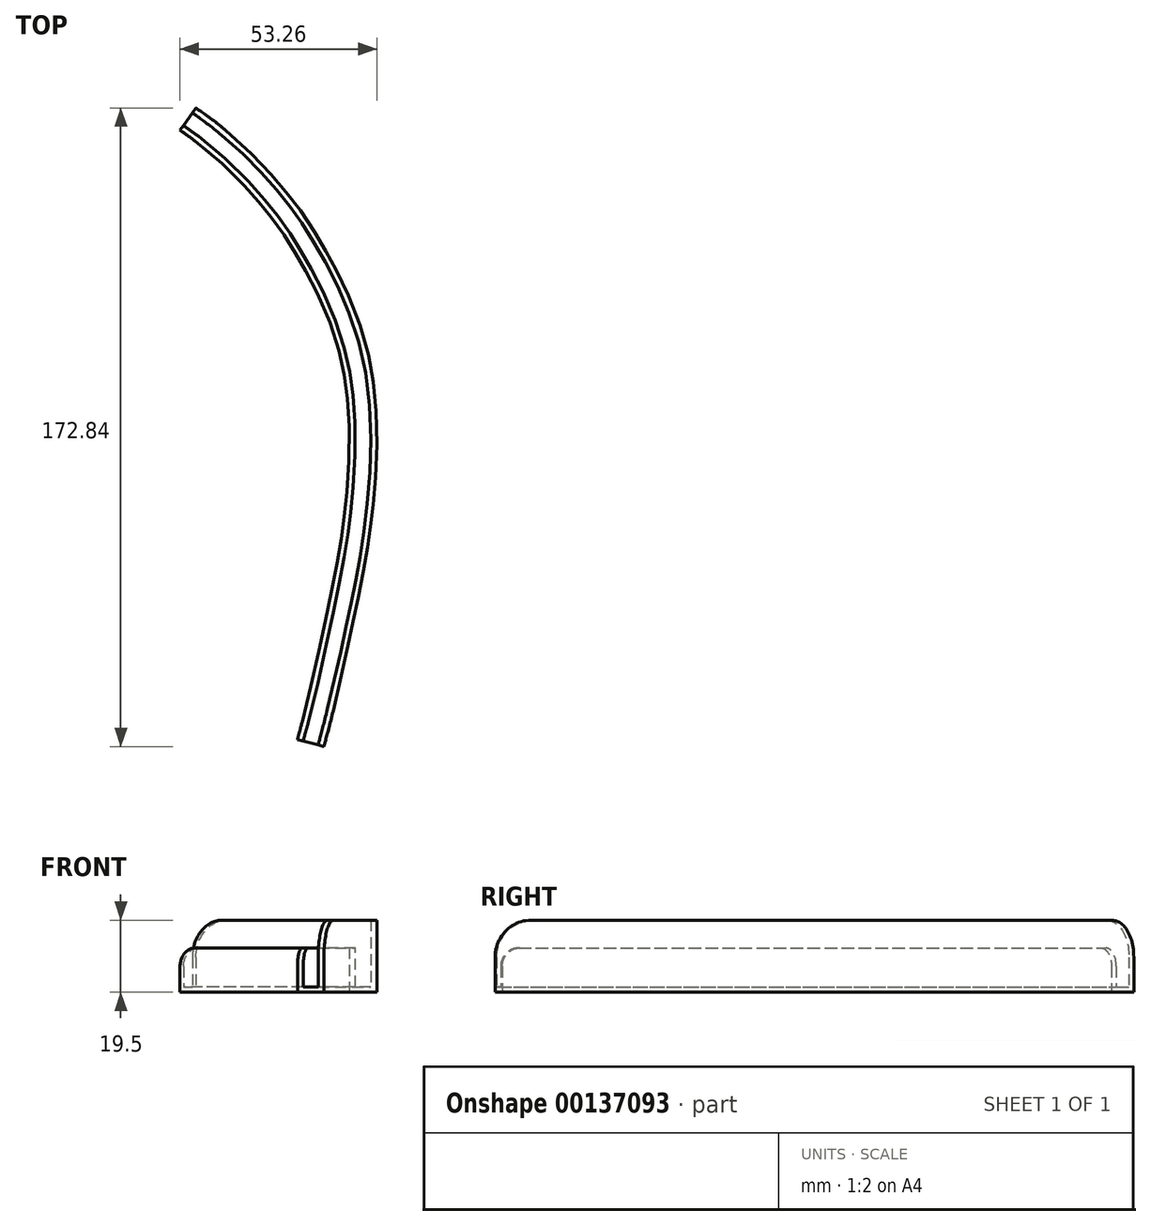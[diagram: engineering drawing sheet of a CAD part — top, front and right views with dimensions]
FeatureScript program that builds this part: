
annotation { "Feature Type Name" : "Feature", "Feature Type Description" : "" }
export const myFeature = defineFeature(function(context is Context, id is Id, definition is map)
    precondition{}
    {
        {
            var Q0;
            Q0=qCreatedBy(makeId("Top.planeOp"),FACE);
            var sketch = newSketch(context, id + "F0", { "sketchPlane" : qUnion([Q0])});
            skFitSpline(sketch, "E0", {"points": [v(0, 0) * mm, v(8.13, 34.88) * mm, v(12.53, 58.96) * mm, v(12.64, 101.94) * mm, v(0, 134.17) * mm, v(-10.91, 149.84) * mm, v(-34.01, 171.11) * mm], "startDerivative": vector(62.8, 232.59) * mm, "endDerivative": vector(-193.61, 137.85) * mm});
            skFitSpline(sketch, "E1.0", {"points": [v(-4.05, 1.1) * mm, v(-2.76, 5.9) * mm, v(-0.5, 14.87) * mm, v(1.7, 24.74) * mm, v(3.23, 31.96) * mm, v(4.3, 37.08) * mm, v(5.33, 41.91) * mm, v(6.29, 46.65) * mm, v(7.03, 50.7) * mm, v(7.59, 54.1) * mm, v(8, 56.75) * mm, v(8.38, 59.54) * mm, v(8.75, 62.48) * mm, v(9.09, 65.56) * mm, v(9.5, 69.82) * mm, v(9.88, 75.37) * mm, v(10.08, 82.26) * mm, v(9.96, 88.05) * mm, v(9.65, 92.64) * mm, v(9.3, 96.03) * mm, v(8.85, 99.35) * mm, v(8.26, 102.58) * mm, v(7.53, 105.74) * mm, v(6.4, 109.85) * mm, v(4.75, 114.8) * mm, v(2.45, 120.37) * mm, v(0.38, 124.68) * mm, v(-1.3, 127.9) * mm, v(-2.56, 130.2) * mm, v(-3.81, 132.39) * mm, v(-5.03, 134.43) * mm, v(-6.23, 136.36) * mm, v(-7.81, 138.8) * mm, v(-9.4, 141.1) * mm, v(-11.09, 143.34) * mm, v(-12.4, 145.02) * mm, v(-13.78, 146.72) * mm, v(-15.73, 149.04) * mm, v(-18.37, 152.02) * mm, v(-21.97, 155.73) * mm, v(-27.47, 160.85) * mm, v(-32.53, 164.9) * mm, v(-36.45, 167.7) * mm]});
            skLineSegment(sketch, "E2", {"start": v(-36.45, 167.7) * mm, "end": v(-34.01, 171.11) * mm});
            skLineSegment(sketch, "E3", {"start": v(0, 0) * mm, "end": v(-4.05, 1.1) * mm});
            skFitSpline(sketch, "E4.0", {"points": [v(1.54, -0.42) * mm, v(2.86, 4.45) * mm, v(4.57, 11.26) * mm, v(6.47, 19.52) * mm, v(7.75, 25.32) * mm, v(8.71, 29.86) * mm, v(9.44, 33.33) * mm, v(10.15, 36.68) * mm, v(11, 40.73) * mm, v(11.98, 45.55) * mm, v(12.74, 49.7) * mm, v(13.32, 53.19) * mm, v(13.73, 55.92) * mm, v(14.13, 58.78) * mm, v(14.5, 61.8) * mm, v(14.86, 64.96) * mm, v(15.28, 69.35) * mm, v(15.68, 75.08) * mm, v(15.88, 82.23) * mm, v(15.73, 89.5) * mm, v(15.23, 95.53) * mm, v(14.58, 100.26) * mm, v(13.73, 104.92) * mm, v(12.3, 110.51) * mm, v(10.18, 116.84) * mm, v(7.75, 122.74) * mm, v(5.58, 127.27) * mm, v(3.81, 130.64) * mm, v(2.5, 133.04) * mm, v(1.2, 135.3) * mm, v(-0.5, 138.15) * mm, v(-2.58, 141.43) * mm, v(-5.12, 145.09) * mm, v(-7.38, 148.04) * mm, v(-9.3, 150.41) * mm, v(-11.34, 152.84) * mm, v(-14.12, 155.97) * mm, v(-17.91, 159.88) * mm, v(-23.7, 165.27) * mm, v(-29, 169.51) * mm, v(-33.08, 172.42) * mm]});
            skFitSpline(sketch, "E5.0", {"points": [v(-5.6, 1.51) * mm, v(-4.3, 6.3) * mm, v(-2.63, 13) * mm, v(-0.75, 21.14) * mm, v(0.51, 26.88) * mm, v(1.66, 32.3) * mm, v(2.74, 37.42) * mm, v(3.76, 42.24) * mm, v(4.71, 46.96) * mm, v(5.45, 50.97) * mm, v(6, 54.34) * mm, v(6.4, 56.98) * mm, v(6.8, 59.75) * mm, v(7.16, 62.67) * mm, v(7.5, 65.72) * mm, v(7.9, 69.95) * mm, v(8.28, 75.45) * mm, v(8.48, 82.27) * mm, v(8.36, 88) * mm, v(8.06, 92.5) * mm, v(7.72, 95.84) * mm, v(7.27, 99.1) * mm, v(6.69, 102.26) * mm, v(5.98, 105.35) * mm, v(4.88, 109.38) * mm, v(3.25, 114.24) * mm, v(0.99, 119.72) * mm, v(-1.05, 123.97) * mm, v(-2.7, 127.15) * mm, v(-3.96, 129.42) * mm, v(-5.2, 131.58) * mm, v(-6.4, 133.6) * mm, v(-7.58, 135.5) * mm, v(-9.14, 137.9) * mm, v(-10.7, 140.16) * mm, v(-12.36, 142.37) * mm, v(-13.65, 144.02) * mm, v(-15.01, 145.7) * mm, v(-16.46, 147.42) * mm, v(-17.98, 149.17) * mm, v(-20.13, 151.54) * mm, v(-23.09, 154.58) * mm, v(-28.5, 159.63) * mm, v(-33.5, 163.63) * mm, v(-37.38, 166.39) * mm]});
            skLineSegment(sketch, "E6", {"start": v(-37.38, 166.39) * mm, "end": v(-36.45, 167.7) * mm});
            skLineSegment(sketch, "E7", {"start": v(-5.6, 1.51) * mm, "end": v(-4.05, 1.1) * mm});
            skLineSegment(sketch, "E8", {"start": v(0, 0) * mm, "end": v(1.54, -0.42) * mm});
            skLineSegment(sketch, "E9", {"start": v(-34.01, 171.11) * mm, "end": v(-33.08, 172.42) * mm});
            skSolve(sketch);
        }
        {
            var Q0;
            Q0=makeQuery(id+"F0.imprint","IMPRINT",FACE,{"disambiguationData":[TD([[makeQuery(id+"F0.imprint","IMPRINT",EDGE,{"derivedFrom":sQuery(id+"F0.wireOp",EDGE,"E1.0")}),1.0]])]});
            var Q1;
            Q1=makeQuery(id+"F0.imprint","IMPRINT",FACE,{"disambiguationData":[TD([[makeQuery(id+"F0.imprint","IMPRINT",EDGE,{"derivedFrom":sQuery(id+"F0.wireOp",EDGE,"E0")}),1.0]])]});
            var Q2;
            Q2=makeQuery(id+"F0.imprint","IMPRINT",FACE,{"disambiguationData":[TD([[makeQuery(id+"F0.imprint","IMPRINT",EDGE,{"derivedFrom":sQuery(id+"F0.wireOp",EDGE,"E0")}),-1.0]])]});
            extrude(context, id + "F1", {"entities" : qUnion([Q0, Q1, Q2]), "depth" : 1.5 * mm});
        }
        {
            var Q0;
            Q0=makeQuery(id+"F0.imprint","IMPRINT",FACE,{"disambiguationData":[TD([[makeQuery(id+"F0.imprint","IMPRINT",EDGE,{"derivedFrom":sQuery(id+"F0.wireOp",EDGE,"E1.0")}),1.0]])]});
            extrude(context, id + "F2", {"entities" : qUnion([Q0]), "operationType" : NewBodyOperationType.ADD, "depth" : 12 * mm});
        }
        {
            var Q0;
            Q0=makeQuery(id+"F0.imprint","IMPRINT",FACE,{"disambiguationData":[TD([[makeQuery(id+"F0.imprint","IMPRINT",EDGE,{"derivedFrom":sQuery(id+"F0.wireOp",EDGE,"E0")}),-1.0]])]});
            extrude(context, id + "F3", {"entities" : qUnion([Q0]), "operationType" : NewBodyOperationType.ADD, "depth" : (18 + 1.5) * mm});
        }
        {
            var Q0;
            Q0=makeQuery(id+"F2.opExtrude","CAP_EDGE",EDGE,{"disambiguationData":[OSD([sQuery(id+"F0.wireOp",EDGE,"E6")])],"isStart":false});
            var Q1;
            Q1=makeQuery(id+"F2.opExtrude","CAP_EDGE",EDGE,{"disambiguationData":[OSD([sQuery(id+"F0.wireOp",EDGE,"E7")])],"isStart":false});
            fillet(context, id + "F4", {"entities" : qUnion([Q0, Q1]), "radius" : 5 * mm, "tangentPropagation" : true, "allowEdgeOverflow" : false});
        }
        {
            var Q0;
            Q0=makeQuery(id+"F3.opExtrude","CAP_EDGE",EDGE,{"disambiguationData":[OSD([sQuery(id+"F0.wireOp",EDGE,"E9")])],"isStart":false});
            var Q1;
            Q1=makeQuery(id+"F3.opExtrude","CAP_EDGE",EDGE,{"disambiguationData":[OSD([sQuery(id+"F0.wireOp",EDGE,"E8")])],"isStart":false});
            fillet(context, id + "F5", {"entities" : qUnion([Q0, Q1]), "radius" : 10 * mm, "tangentPropagation" : true, "allowEdgeOverflow" : false});
        }
    });
